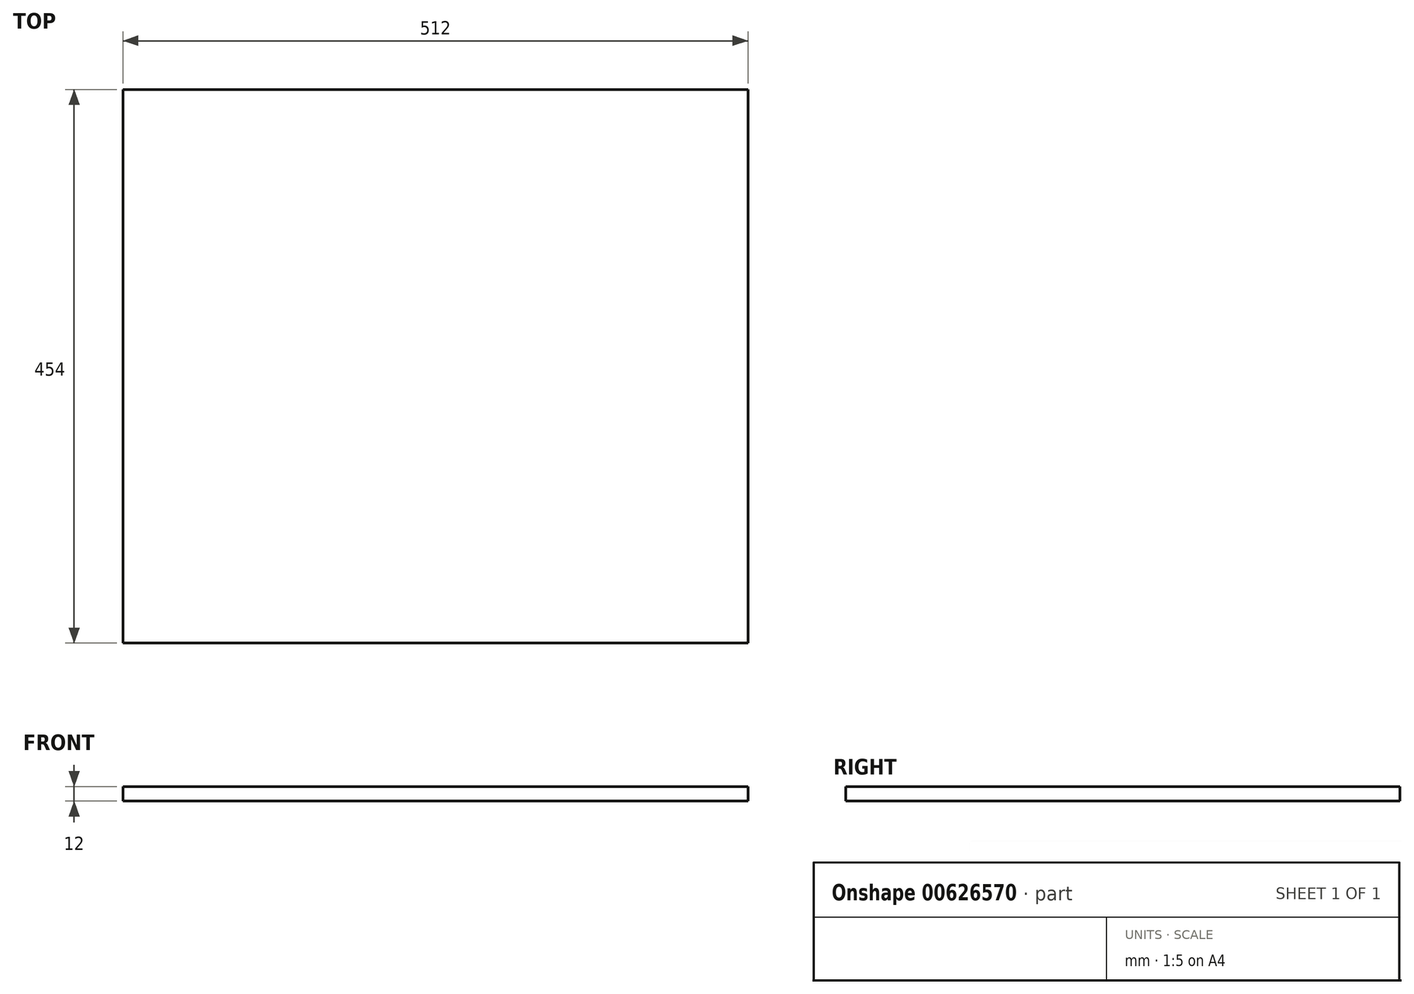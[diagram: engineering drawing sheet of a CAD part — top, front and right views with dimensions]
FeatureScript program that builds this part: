
annotation { "Feature Type Name" : "Feature", "Feature Type Description" : "" }
export const myFeature = defineFeature(function(context is Context, id is Id, definition is map)
    precondition{}
    {
        {
            assignVariable(context, id + "F0", {"name" : "thickness", "anyValue" : 12});
        }
        {
            var Q0;
            Q0=qCreatedBy(makeId("Top.planeOp"),FACE);
            var sketch = newSketch(context, id + "F1", { "sketchPlane" : qUnion([Q0])});
            skLineSegment(sketch, "E0.bottom", {"start": v(256, -227) * mm, "end": v(-256, -227) * mm});
            skLineSegment(sketch, "E0.top", {"start": v(256, 227) * mm, "end": v(-256, 227) * mm});
            skLineSegment(sketch, "E0.left", {"start": v(256, -227) * mm, "end": v(256, 227) * mm});
            skLineSegment(sketch, "E0.right", {"start": v(-256, -227) * mm, "end": v(-256, 227) * mm});
            skPoint(sketch, "E0.middle", {"position": v(0, 0) * mm});
            skSolve(sketch);
        }
        {
            var Q0;
            Q0=qSketchRegion(id+"F1",true);
            extrude(context, id + "F2", {"entities" : qUnion([Q0]), "depth" : (getVariable(context, 'thickness')) * mm});
        }
    });
